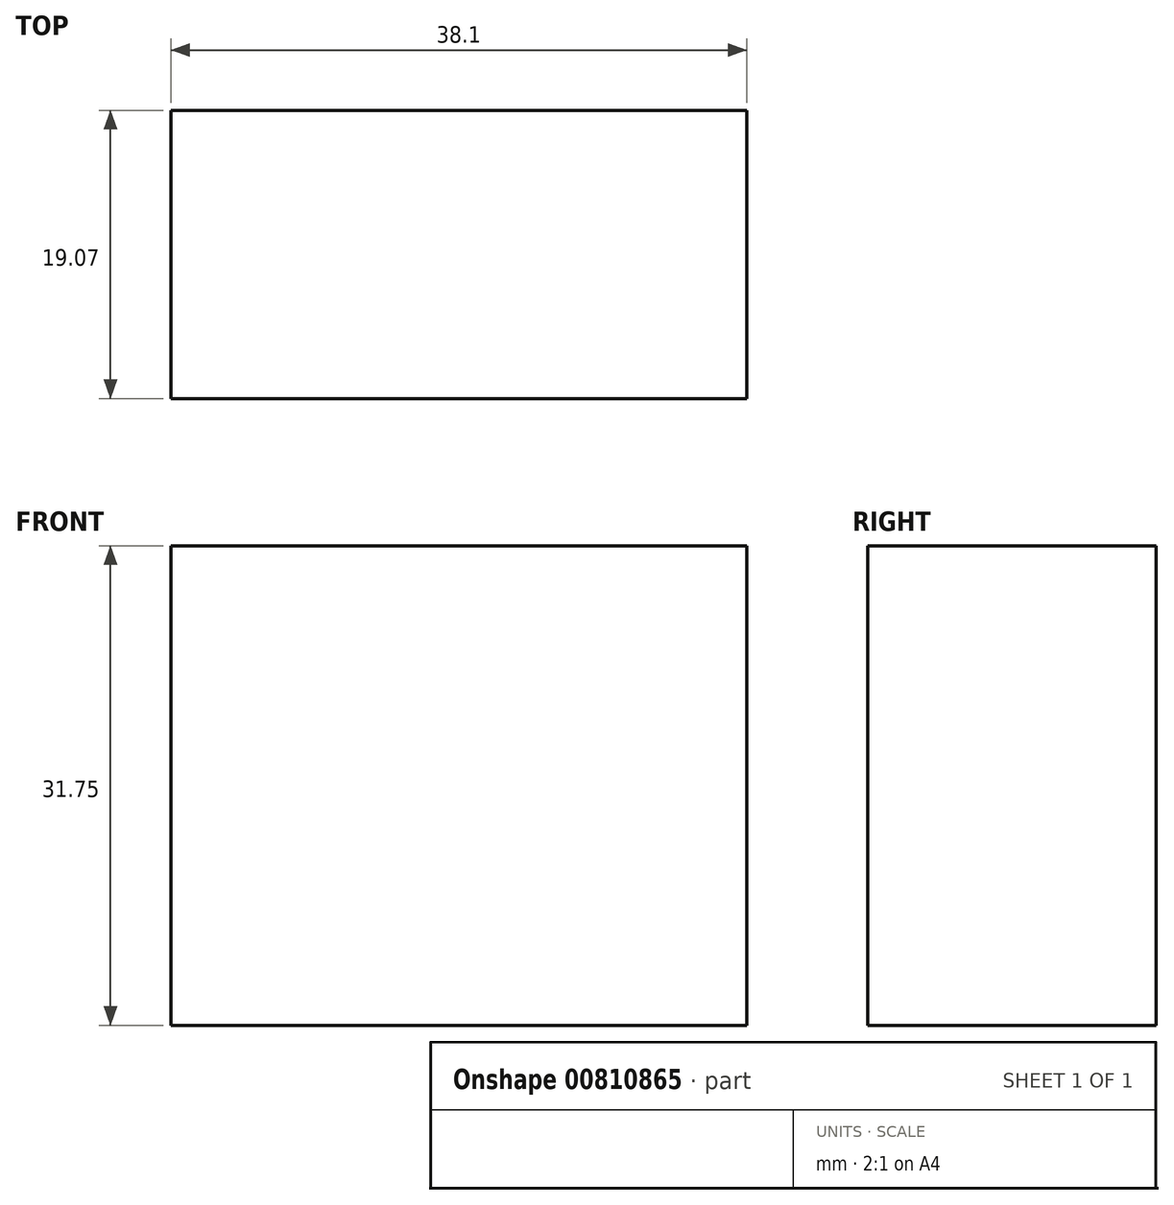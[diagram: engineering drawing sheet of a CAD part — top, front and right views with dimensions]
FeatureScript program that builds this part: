
annotation { "Feature Type Name" : "Feature", "Feature Type Description" : "" }
export const myFeature = defineFeature(function(context is Context, id is Id, definition is map)
    precondition{}
    {
        {
            var Q0;
            Q0=qCreatedBy(makeId("Top.planeOp"),FACE);
            var sketch = newSketch(context, id + "F0", { "sketchPlane" : qUnion([Q0])});
            skLineSegment(sketch, "E0.bottom", {"start": v(0, 0) * mm, "end": v(38.1, 0) * mm});
            skLineSegment(sketch, "E0.top", {"start": v(0, 19.07) * mm, "end": v(38.1, 19.07) * mm});
            skLineSegment(sketch, "E0.left", {"start": v(0, 0) * mm, "end": v(0, 19.07) * mm});
            skLineSegment(sketch, "E0.right", {"start": v(38.1, 0) * mm, "end": v(38.1, 19.07) * mm});
            skSolve(sketch);
        }
        {
            var Q0;
            Q0 = qSketchRegion(id + "F0", true);
            extrude(context, id + "F1", {"entities" : qUnion([Q0]), "depth" : 31.75 * mm, "offsetDistance" : 25.4 * mm});
        }
    });
